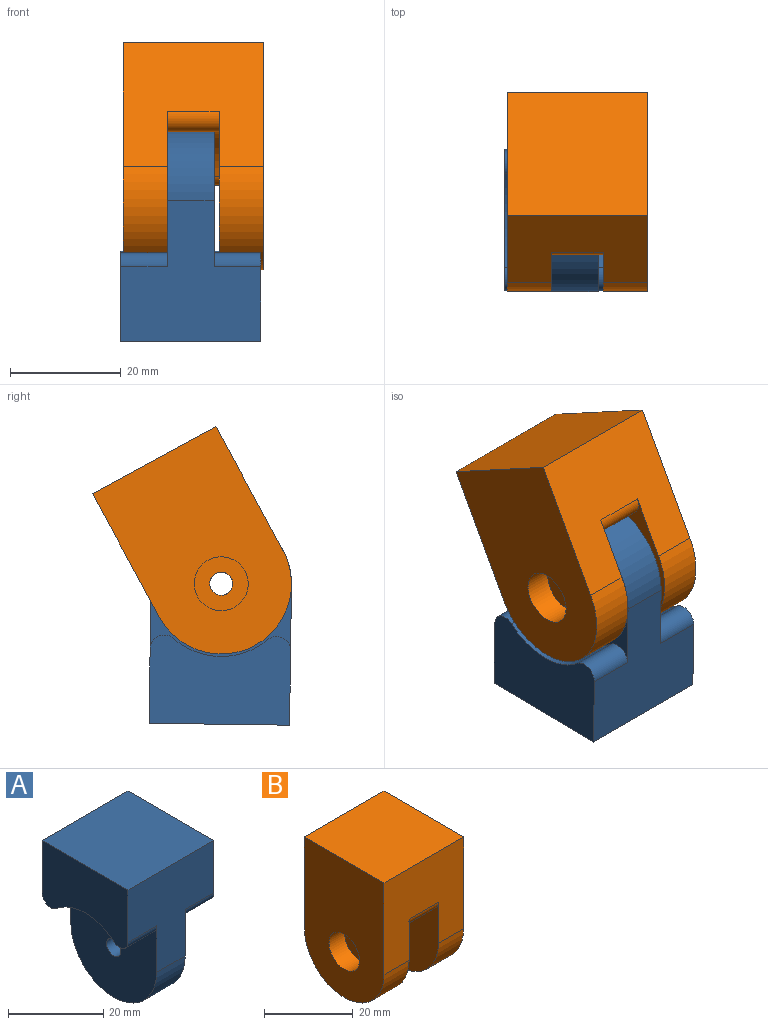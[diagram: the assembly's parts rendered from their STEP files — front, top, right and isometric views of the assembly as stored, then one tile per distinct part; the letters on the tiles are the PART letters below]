
ASSEMBLY  parts=2 mates=1
PART A: 15 faces, bbox 25.4x25.4x38.1 mm
  f0: plane 25.4x15.98mm, normal (1,0,0), area 355.8mm2, adj f1,f3,f4,f8,f11,f13
  f1: plane 25.4x25.4mm, normal (0,1,0), area 442.7mm2, adj f0,f2,f4,f5,f6,f7,f10,f11
  f2: plane 25.4x15.98mm, normal (-1,0,0), area 355.8mm2, adj f1,f3,f4,f9,f10,f12
  f3: plane 25.4x25.4mm, normal (0,-1,0), area 442.7mm2, adj f0,f2,f4,f5,f6,f7,f12,f13
  f4: plane 25.4x25.4mm, normal (0,0,1), area 645.2mm2, adj f0,f1,f2,f3
  f5: plane 25.85x25.4mm, normal (1,0,0), area 528.8mm2, adj f1,f3,f6,f8,f11,f13,f14
  f6: cylinder r=12.7mm len=25.4mm, axis (-1,0,0), area 337.8mm2, adj f1,f3,f5,f7
  f7: plane 25.85x25.4mm, normal (-1,0,0), area 528.8mm2, adj f1,f3,f6,f9,f10,f12,f14
  f8: cylinder r=13.15mm len=17.03mm, axis (1,0,0), area 156.8mm2, adj f0,f5,f11,f13
  f9: cylinder r=13.15mm len=17.03mm, axis (1,0,0), area 156.8mm2, adj f2,f7,f10,f12
  f10: cylinder r=2.54mm len=8.47mm, axis (1,0,0), area 48.9mm2, adj f1,f2,f7,f9
  f11: cylinder r=2.54mm len=8.47mm, axis (1,0,0), area 48.9mm2, adj f0,f1,f5,f8
  f12: cylinder r=2.54mm len=8.47mm, axis (1,0,0), area 48.9mm2, adj f2,f3,f7,f9
  f13: cylinder r=2.54mm len=8.47mm, axis (1,0,0), area 48.9mm2, adj f0,f3,f5,f8
  f14: cylinder r=2.1mm len=8.47mm, axis (-1,0,0), area 111.7mm2, adj f5,f7
PART B: 16 faces, bbox 25.4x25.4x38.1 mm
  f0: plane 25.4x25.4mm, normal (0,-1,0), area 538.8mm2, adj f1,f3,f5,f6,f8,f10,f14,f15
  f1: cylinder r=12.7mm len=25.4mm, axis (1,0,0), area 319.9mm2, adj f0,f3,f4,f14
  f2: cylinder r=2.1mm len=4.2mm, axis (-1,0,0), area 39.8mm2, adj f12,f15
  f3: plane 38.1x25.4mm, normal (1,0,0), area 884.7mm2, adj f0,f1,f4,f6,f13
  f4: plane 25.4x25.4mm, normal (0,1,0), area 538.8mm2, adj f1,f3,f5,f6,f8,f9,f14,f15
  f5: plane 38.1x25.4mm, normal (-1,0,0), area 823.9mm2, adj f0,f4,f6,f8,f11
  f6: plane 25.4x25.4mm, normal (0,0,1), area 645.2mm2, adj f0,f3,f4,f5
  f7: cylinder r=12.7mm len=16.93mm, axis (-1,0,0), area 173.6mm2, adj f9,f10,f14,f15
  f8: cylinder r=12.7mm len=25.4mm, axis (1,0,0), area 319.9mm2, adj f0,f4,f5,f15
  f9: cylinder r=2.54mm len=9.37mm, axis (-1,0,0), area 54.7mm2, adj f4,f7,f14,f15
  f10: cylinder r=2.54mm len=9.37mm, axis (-1,0,0), area 54.7mm2, adj f0,f7,f14,f15
  f11: cylinder r=4.88mm len=9.75mm, axis (-1,0,0), area 153.2mm2, adj f5,f12
  f12: plane 9.75x9.75mm, normal (-1,0,0), area 60.8mm2, adj f2,f11
  f13: cylinder r=2.1mm len=8.02mm, axis (-1,0,0), area 105.8mm2, adj f3,f14
  f14: plane 25.4x25.4mm, normal (-1,0,0), area 515.5mm2, adj f0,f1,f4,f7,f9,f10,f13
  f15: plane 25.4x25.4mm, normal (1,0,0), area 515.5mm2, adj f0,f2,f4,f7,f8,f9,f10
PLACE A rot(axis=(-1,0,0),179.2deg) t=(5.64,9.32,2.35)mm fixed
PLACE B rot(axis=(-1,0,0),28.5deg) t=(6.09,9.32,2.35)mm
MATE revolute A.f6 <-> B.f2  axis (-1,0,0) through (1.41,9.32,2.35)mm
